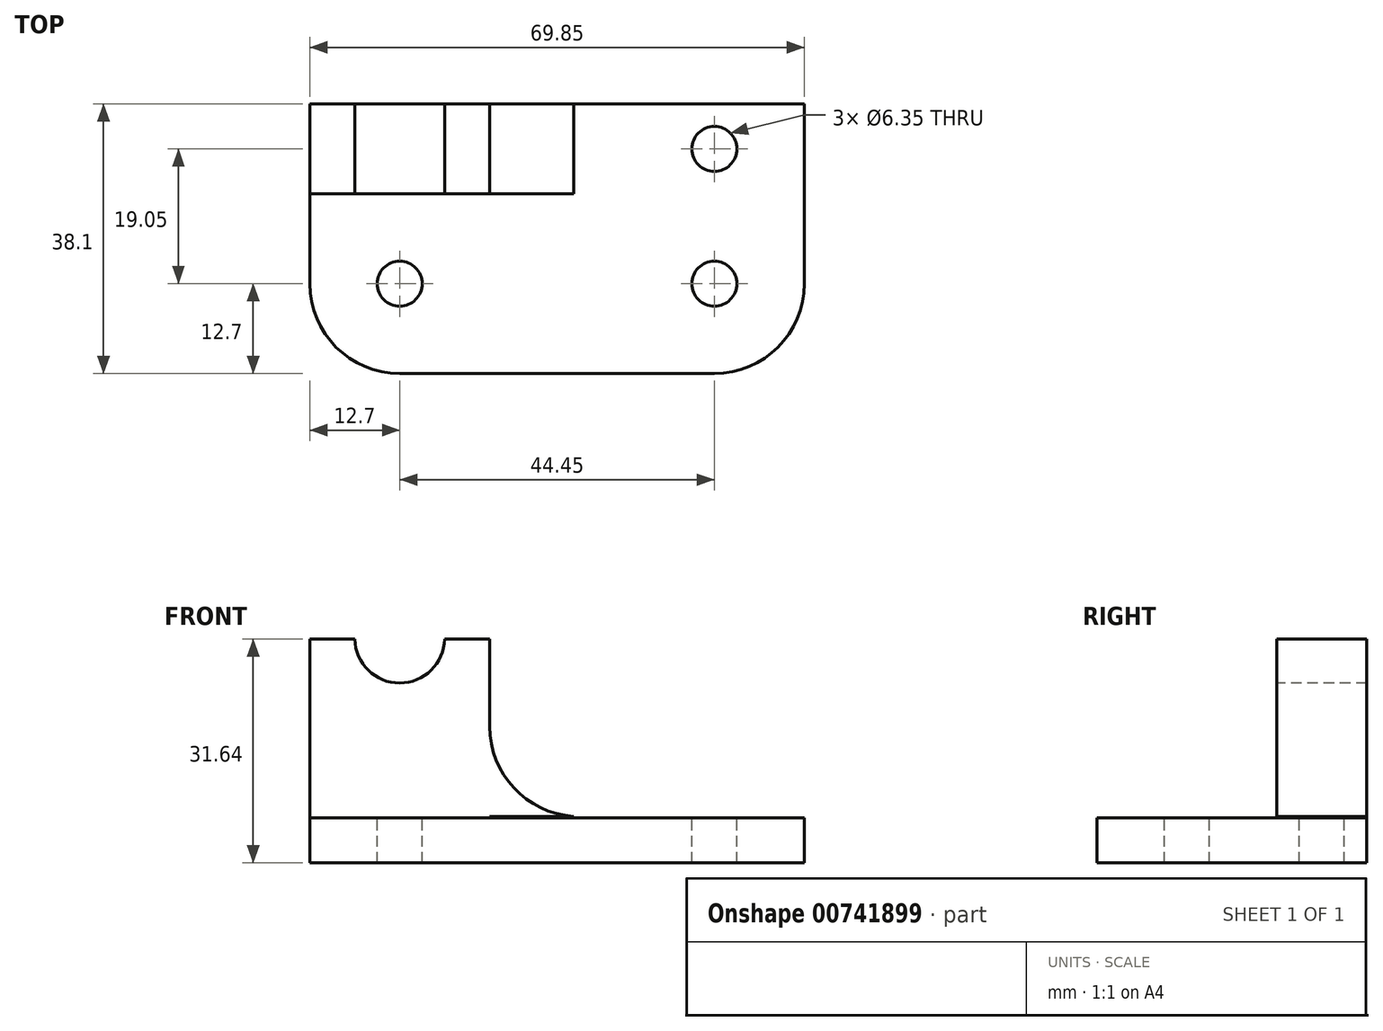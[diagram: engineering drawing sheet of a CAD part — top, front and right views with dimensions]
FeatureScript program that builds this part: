
annotation { "Feature Type Name" : "Feature", "Feature Type Description" : "" }
export const myFeature = defineFeature(function(context is Context, id is Id, definition is map)
    precondition{}
    {
        {
            var Q0;
            Q0=qCreatedBy(makeId("Front.planeOp"),FACE);
            var sketch = newSketch(context, id + "F0", { "sketchPlane" : qUnion([Q0])});
            skLineSegment(sketch, "E0", {"start": v(0, 44.45) * mm, "end": v(0, 0) * mm});
            skLineSegment(sketch, "E1", {"start": v(0, 0) * mm, "end": v(69.85, 0) * mm});
            skLineSegment(sketch, "E2", {"start": v(69.85, 0) * mm, "end": v(69.85, 6.35) * mm});
            skLineSegment(sketch, "E3", {"start": v(69.85, 6.35) * mm, "end": v(25.4, 6.35) * mm});
            skLineSegment(sketch, "E4", {"start": v(25.4, 6.35) * mm, "end": v(25.4, 44.45) * mm});
            skLineSegment(sketch, "E5", {"start": v(25.4, 44.45) * mm, "end": v(0, 44.45) * mm});
            skSolve(sketch);
        }
        {
            var Q0;
            Q0=makeQuery(id+"F0.imprint","IMPRINT",FACE,{"disambiguationData":[TD([[makeQuery(id+"F0.imprint","IMPRINT",EDGE,{"derivedFrom":sQuery(id+"F0.wireOp",EDGE,"E0")}),1.0]])]});
            extrude(context, id + "F1", {"entities" : qUnion([Q0]), "depth" : 38.1 * mm, "offsetDistance" : 25.4 * mm});
        }
        {
            var Q0;
            Q0=makeQuery(id+"F1.opExtrude","CAP_FACE",FACE,{"disambiguationData":[OSD([sQuery(id+"F0.wireOp",EDGE,"E0"),sQuery(id+"F0.wireOp",EDGE,"E1"),sQuery(id+"F0.wireOp",EDGE,"E2"),sQuery(id+"F0.wireOp",EDGE,"E3"),sQuery(id+"F0.wireOp",EDGE,"E4"),sQuery(id+"F0.wireOp",EDGE,"E5")])],"isStart":false});
            var sketch = newSketch(context, id + "F2", { "sketchPlane" : qUnion([Q0])});
            skLineSegment(sketch, "E6", {"start": v(0, 44.45) * mm, "end": v(0, 6.35) * mm});
            skLineSegment(sketch, "E7", {"start": v(0, 6.35) * mm, "end": v(25.4, 6.35) * mm});
            skLineSegment(sketch, "E8", {"start": v(25.4, 6.35) * mm, "end": v(25.4, 44.45) * mm});
            skLineSegment(sketch, "E9", {"start": v(25.4, 44.45) * mm, "end": v(0, 44.45) * mm});
            skSolve(sketch);
        }
        {
            var Q0;
            Q0=makeQuery(id+"F2.imprint","IMPRINT",FACE,{"disambiguationData":[TD([[makeQuery(id+"F2.imprint","IMPRINT",EDGE,{"derivedFrom":sQuery(id+"F2.wireOp",EDGE,"E6")}),1.0]])]});
            extrude(context, id + "F3", {"entities" : qUnion([Q0]), "operationType" : NewBodyOperationType.REMOVE, "oppositeDirection" : true, "depth" : 25.4 * mm, "offsetDistance" : 25.4 * mm});
        }
        {
            var Q0;
            Q0=makeQuery(id+"F3.boolean.opBoolean","COPY",FACE,{"derivedFrom":makeQuery(id+"F3.opExtrude","CAP_FACE",FACE,{"disambiguationData":[OSD([sQuery(id+"F2.wireOp",EDGE,"E6"),sQuery(id+"F2.wireOp",EDGE,"E7"),sQuery(id+"F2.wireOp",EDGE,"E8"),sQuery(id+"F2.wireOp",EDGE,"E9")])],"isStart":false})});
            var sketch = newSketch(context, id + "F4", { "sketchPlane" : qUnion([Q0])});
            skCircle(sketch, "E10", {"center": v(12.7, 31.75) * mm, "radius": 6.35 * mm});
            skSolve(sketch);
        }
        {
            var Q0;
            Q0=makeQuery(id+"F4.imprint","IMPRINT",FACE,{"disambiguationData":[TD([[makeQuery(id+"F4.imprint","IMPRINT",EDGE,{"derivedFrom":sQuery(id+"F4.wireOp",EDGE,"E10")}),1.0]])]});
            extrude(context, id + "F5", {"entities" : qUnion([Q0]), "operationType" : NewBodyOperationType.REMOVE, "endBound" : BoundingType.THROUGH_ALL, "oppositeDirection" : true, "depth" : 25.4 * mm, "offsetDistance" : 25.4 * mm});
        }
        {
            var Q0;
            Q0=makeQuery(id+"F3.boolean.opBoolean","COPY",FACE,{"derivedFrom":makeQuery(id+"F3.opExtrude","CAP_FACE",FACE,{"disambiguationData":[OSD([sQuery(id+"F2.wireOp",EDGE,"E6"),sQuery(id+"F2.wireOp",EDGE,"E7"),sQuery(id+"F2.wireOp",EDGE,"E8"),sQuery(id+"F2.wireOp",EDGE,"E9")])],"isStart":false})});
            var sketch = newSketch(context, id + "F6", { "sketchPlane" : qUnion([Q0])});
            skLineSegment(sketch, "E11", {"start": v(0, 31.64) * mm, "end": v(25.4, 31.64) * mm});
            skArc(sketch, "E12", {"start": v(25.4, 31.64) * mm, "mid": v(12.7, 44.74) * mm, "end": v(0, 31.64) * mm});
            skSolve(sketch);
        }
        {
            var Q0;
            {var subQ0=sQuery(id+"F6.wireOp",EDGE,"E12");var subQ1=makeQuery(id+"F3.boolean.opBoolean","COPY",EDGE,{"derivedFrom":makeQuery(id+"F3.opExtrude","CAP_EDGE",EDGE,{"disambiguationData":[OSD([sQuery(id+"F2.wireOp",EDGE,"E8")])],"isStart":false})});var subQ3=makeQuery(id+"F6.imprint","INTERSECT",VERTEX,{"derivedFrom":[subQ1,subQ0]});Q0=makeQuery(id+"F6.imprint","IMPRINT",FACE,{"disambiguationData":[TD([[makeQuery(id+"F6.imprint","IMPRINT",EDGE,{"disambiguationData":[TD([[subQ3,1.0]])],"derivedFrom":subQ0}),1.0]])]});}
            var Q1;
            {var subQ0=sQuery(id+"F6.wireOp",EDGE,"E12");var subQ1=makeQuery(id+"F3.boolean.opBoolean","COPY",EDGE,{"derivedFrom":makeQuery(id+"F3.opExtrude","CAP_EDGE",EDGE,{"disambiguationData":[OSD([sQuery(id+"F2.wireOp",EDGE,"E9")])],"isStart":false})});var subQ2=makeQuery(id+"F6.imprint","INTERSECT",VERTEX,{"disambiguationData":[OD(0.0)],"derivedFrom":[subQ1,subQ0]});Q1=makeQuery(id+"F6.imprint","IMPRINT",FACE,{"disambiguationData":[TD([[makeQuery(id+"F6.imprint","IMPRINT",EDGE,{"disambiguationData":[TD([[subQ2,-1.0]])],"derivedFrom":subQ0}),1.0]])]});}
            var Q2;
            {var subQ0=sQuery(id+"F6.wireOp",EDGE,"E12");var subQ1=makeQuery(id+"F3.boolean.opBoolean","COPY",EDGE,{"derivedFrom":makeQuery(id+"F3.opExtrude","CAP_EDGE",EDGE,{"disambiguationData":[OSD([sQuery(id+"F2.wireOp",EDGE,"E6")])],"isStart":false})});var subQ3=makeQuery(id+"F6.imprint","INTERSECT",VERTEX,{"derivedFrom":[subQ1,subQ0]});Q2=makeQuery(id+"F6.imprint","IMPRINT",FACE,{"disambiguationData":[TD([[makeQuery(id+"F6.imprint","IMPRINT",EDGE,{"disambiguationData":[TD([[subQ3,-1.0]])],"derivedFrom":subQ0}),1.0]])]});}
            var Q3;
            {var subQ0=sQuery(id+"F6.wireOp",EDGE,"E11");var subQ1=makeQuery(id+"F5.boolean.opBoolean","COPY",EDGE,{"derivedFrom":makeQuery(id+"F5.opExtrude","CAP_EDGE",EDGE,{"disambiguationData":[OSD([sQuery(id+"F4.wireOp",EDGE,"E10")])],"isStart":true})});var subQ2=makeQuery(id+"F6.imprint","INTERSECT",VERTEX,{"disambiguationData":[OD(0.0)],"derivedFrom":[subQ1,subQ0]});Q3=makeQuery(id+"F6.imprint","IMPRINT",FACE,{"disambiguationData":[TD([[makeQuery(id+"F6.imprint","IMPRINT",EDGE,{"disambiguationData":[TD([[subQ2,-1.0]])],"derivedFrom":subQ0}),1.0]])]});}
            var Q4;
            {var subQ0=sQuery(id+"F6.wireOp",EDGE,"E12");var subQ1=makeQuery(id+"F3.boolean.opBoolean","COPY",EDGE,{"derivedFrom":makeQuery(id+"F3.opExtrude","CAP_EDGE",EDGE,{"disambiguationData":[OSD([sQuery(id+"F2.wireOp",EDGE,"E9")])],"isStart":false})});var subQ2=makeQuery(id+"F6.imprint","INTERSECT",VERTEX,{"disambiguationData":[OD(1.0)],"derivedFrom":[subQ1,subQ0]});Q4=makeQuery(id+"F6.imprint","IMPRINT",FACE,{"disambiguationData":[TD([[makeQuery(id+"F6.imprint","IMPRINT",EDGE,{"disambiguationData":[TD([[subQ2,-1.0]])],"derivedFrom":subQ0}),-1.0]])]});}
            var Q5;
            {var subQ0=sQuery(id+"F6.wireOp",EDGE,"E12");var subQ1=makeQuery(id+"F3.boolean.opBoolean","COPY",EDGE,{"derivedFrom":makeQuery(id+"F3.opExtrude","CAP_EDGE",EDGE,{"disambiguationData":[OSD([sQuery(id+"F2.wireOp",EDGE,"E8")])],"isStart":false})});var subQ2=makeQuery(id+"F6.imprint","INTERSECT",VERTEX,{"derivedFrom":[subQ1,subQ0]});Q5=makeQuery(id+"F6.imprint","IMPRINT",FACE,{"disambiguationData":[TD([[makeQuery(id+"F6.imprint","IMPRINT",EDGE,{"disambiguationData":[TD([[subQ2,-1.0]])],"derivedFrom":subQ0}),-1.0]])]});}
            extrude(context, id + "F7", {"entities" : qUnion([Q0, Q1, Q2, Q3, Q4, Q5]), "operationType" : NewBodyOperationType.REMOVE, "endBound" : BoundingType.THROUGH_ALL, "oppositeDirection" : true, "depth" : 25.4 * mm, "offsetDistance" : 25.4 * mm});
        }
        {
            var Q0;
            Q0=qCreatedBy(makeId("Front.planeOp"),FACE);
            var sketch = newSketch(context, id + "F8", { "sketchPlane" : qUnion([Q0])});
            skLineSegment(sketch, "E13", {"start": v(24.56, 6.56) * mm, "end": v(24.56, 19.26) * mm});
            skLineSegment(sketch, "E14", {"start": v(24.56, 19.26) * mm, "end": v(37.26, 19.26) * mm});
            skLineSegment(sketch, "E15", {"start": v(37.26, 19.26) * mm, "end": v(37.26, 6.56) * mm});
            skLineSegment(sketch, "E16", {"start": v(37.26, 6.56) * mm, "end": v(24.56, 6.56) * mm});
            skSolve(sketch);
        }
        {
            var Q0;
            Q0=makeQuery(id+"F8.imprint","IMPRINT",FACE,{"disambiguationData":[TD([[makeQuery(id+"F8.imprint","IMPRINT",EDGE,{"derivedFrom":sQuery(id+"F8.wireOp",EDGE,"E13")}),-1.0]])]});
            extrude(context, id + "F9", {"entities" : qUnion([Q0]), "operationType" : NewBodyOperationType.ADD, "depth" : 12.7 * mm, "offsetDistance" : 25.4 * mm});
        }
        {
            var Q0;
            Q0=makeQuery(id+"F9.boolean.opBoolean","MERGE",FACE,{"derivedFrom":[makeQuery(id+"F3.boolean.opBoolean","COPY",FACE,{"derivedFrom":makeQuery(id+"F3.opExtrude","CAP_FACE",FACE,{"disambiguationData":[OSD([sQuery(id+"F2.wireOp",EDGE,"E6"),sQuery(id+"F2.wireOp",EDGE,"E7"),sQuery(id+"F2.wireOp",EDGE,"E8"),sQuery(id+"F2.wireOp",EDGE,"E9")])],"isStart":false})}),makeQuery(id+"F9.opExtrude","CAP_FACE",FACE,{"disambiguationData":[OSD([sQuery(id+"F8.wireOp",EDGE,"E13"),sQuery(id+"F8.wireOp",EDGE,"E14"),sQuery(id+"F8.wireOp",EDGE,"E15"),sQuery(id+"F8.wireOp",EDGE,"E16")])],"isStart":false})]});
            var sketch = newSketch(context, id + "F10", { "sketchPlane" : qUnion([Q0])});
            skArc(sketch, "E17", {"start": v(25.4, 19.26) * mm, "mid": v(28.83, 10.57) * mm, "end": v(37.26, 6.56) * mm});
            skSolve(sketch);
        }
        {
            var Q0;
            Q0=makeQuery(id+"F10.imprint","IMPRINT",FACE,{"disambiguationData":[TD([[makeQuery(id+"F10.imprint","IMPRINT",EDGE,{"derivedFrom":sQuery(id+"F10.wireOp",EDGE,"E17")}),1.0]])]});
            extrude(context, id + "F11", {"entities" : qUnion([Q0]), "operationType" : NewBodyOperationType.REMOVE, "endBound" : BoundingType.THROUGH_ALL, "oppositeDirection" : true, "depth" : 25.4 * mm, "offsetDistance" : 25.4 * mm});
        }
        {
            var Q0;
            Q0=makeQuery(id+"F3.boolean.opBoolean","MERGE",FACE,{"derivedFrom":[makeQuery(id+"F1.opExtrude","SWEPT_FACE",FACE,{"disambiguationData":[OSD([sQuery(id+"F0.wireOp",EDGE,"E3")])]}),makeQuery(id+"F3.opExtrude","SWEPT_FACE",FACE,{"disambiguationData":[OSD([sQuery(id+"F2.wireOp",EDGE,"E7")])]})]});
            var sketch = newSketch(context, id + "F12", { "sketchPlane" : qUnion([Q0])});
            skLineSegment(sketch, "E18", {"start": v(0, -25.4) * mm, "end": v(0, -38.1) * mm});
            skLineSegment(sketch, "E19", {"start": v(0, -38.1) * mm, "end": v(12.7, -38.1) * mm});
            skLineSegment(sketch, "E20", {"start": v(69.85, -25.4) * mm, "end": v(69.85, -38.1) * mm});
            skLineSegment(sketch, "E21", {"start": v(69.85, -38.1) * mm, "end": v(57.15, -38.1) * mm});
            skArc(sketch, "E22", {"start": v(0, -25.4) * mm, "mid": v(3.72, -34.38) * mm, "end": v(12.7, -38.1) * mm});
            skArc(sketch, "E23", {"start": v(57.15, -38.1) * mm, "mid": v(66.13, -34.38) * mm, "end": v(69.85, -25.4) * mm});
            skSolve(sketch);
        }
        {
            var Q0;
            Q0=makeQuery(id+"F12.imprint","IMPRINT",FACE,{"disambiguationData":[TD([[makeQuery(id+"F12.imprint","IMPRINT",EDGE,{"derivedFrom":sQuery(id+"F12.wireOp",EDGE,"E18")}),1.0]])]});
            var Q1;
            Q1=makeQuery(id+"F12.imprint","IMPRINT",FACE,{"disambiguationData":[TD([[makeQuery(id+"F12.imprint","IMPRINT",EDGE,{"derivedFrom":sQuery(id+"F12.wireOp",EDGE,"E20")}),1.0]])]});
            extrude(context, id + "F13", {"entities" : qUnion([Q0, Q1]), "operationType" : NewBodyOperationType.REMOVE, "endBound" : BoundingType.THROUGH_ALL, "oppositeDirection" : true, "depth" : 25.4 * mm, "offsetDistance" : 25.4 * mm});
        }
        {
            var Q0;
            Q0=makeQuery(id+"F3.boolean.opBoolean","MERGE",FACE,{"derivedFrom":[makeQuery(id+"F1.opExtrude","SWEPT_FACE",FACE,{"disambiguationData":[OSD([sQuery(id+"F0.wireOp",EDGE,"E3")])]}),makeQuery(id+"F3.opExtrude","SWEPT_FACE",FACE,{"disambiguationData":[OSD([sQuery(id+"F2.wireOp",EDGE,"E7")])]})]});
            var sketch = newSketch(context, id + "F14", { "sketchPlane" : qUnion([Q0])});
            skLineSegment(sketch, "E24", {"start": v(69.85, 0) * mm, "end": v(69.85, -12.7) * mm});
            skLineSegment(sketch, "E25", {"start": v(69.85, -12.7) * mm, "end": v(69.85, 0) * mm});
            skLineSegment(sketch, "E26", {"start": v(69.85, 0) * mm, "end": v(57.15, 0) * mm});
            skLineSegment(sketch, "E27", {"start": v(57.15, 0) * mm, "end": v(57.15, -12.7) * mm});
            skCircle(sketch, "E28", {"center": v(57.15, -6.35) * mm, "radius": 3.18 * mm});
            skLineSegment(sketch, "E29", {"start": v(0, -25.4) * mm, "end": v(12.7, -25.4) * mm});
            skCircle(sketch, "E30", {"center": v(12.7, -25.4) * mm, "radius": 3.18 * mm});
            skLineSegment(sketch, "E31", {"start": v(69.85, -25.4) * mm, "end": v(57.15, -25.4) * mm});
            skCircle(sketch, "E32", {"center": v(57.15, -25.4) * mm, "radius": 3.18 * mm});
            skSolve(sketch);
        }
        {
            var Q0;
            Q0=makeQuery(id+"F14.imprint","IMPRINT",FACE,{"disambiguationData":[TD([[makeQuery(id+"F14.imprint","IMPRINT",EDGE,{"derivedFrom":sQuery(id+"F14.wireOp",EDGE,"E30")}),1.0]])]});
            var Q1;
            Q1=makeQuery(id+"F14.imprint","IMPRINT",FACE,{"disambiguationData":[TD([[makeQuery(id+"F14.imprint","IMPRINT",EDGE,{"derivedFrom":sQuery(id+"F14.wireOp",EDGE,"E32")}),1.0]])]});
            var Q2;
            {var subQ0=sQuery(id+"F14.wireOp",EDGE,"E28");var subQ1=sQuery(id+"F14.wireOp",EDGE,"E27");var subQ2=makeQuery(id+"F14.imprint","INTERSECT",VERTEX,{"disambiguationData":[OD(0.0)],"derivedFrom":[subQ1,subQ0]});Q2=makeQuery(id+"F14.imprint","IMPRINT",FACE,{"disambiguationData":[TD([[makeQuery(id+"F14.imprint","IMPRINT",EDGE,{"disambiguationData":[TD([[subQ2,1.0]])],"derivedFrom":subQ1}),-1.0]])]});}
            var Q3;
            {var subQ0=sQuery(id+"F14.wireOp",EDGE,"E28");var subQ1=sQuery(id+"F14.wireOp",EDGE,"E27");var subQ2=makeQuery(id+"F14.imprint","INTERSECT",VERTEX,{"disambiguationData":[OD(0.0)],"derivedFrom":[subQ1,subQ0]});Q3=makeQuery(id+"F14.imprint","IMPRINT",FACE,{"disambiguationData":[TD([[makeQuery(id+"F14.imprint","IMPRINT",EDGE,{"disambiguationData":[TD([[subQ2,1.0]])],"derivedFrom":subQ1}),1.0]])]});}
            extrude(context, id + "F15", {"entities" : qUnion([Q0, Q1, Q2, Q3]), "operationType" : NewBodyOperationType.REMOVE, "endBound" : BoundingType.THROUGH_ALL, "oppositeDirection" : true, "depth" : 25.4 * mm, "offsetDistance" : 25.4 * mm});
        }
    });
